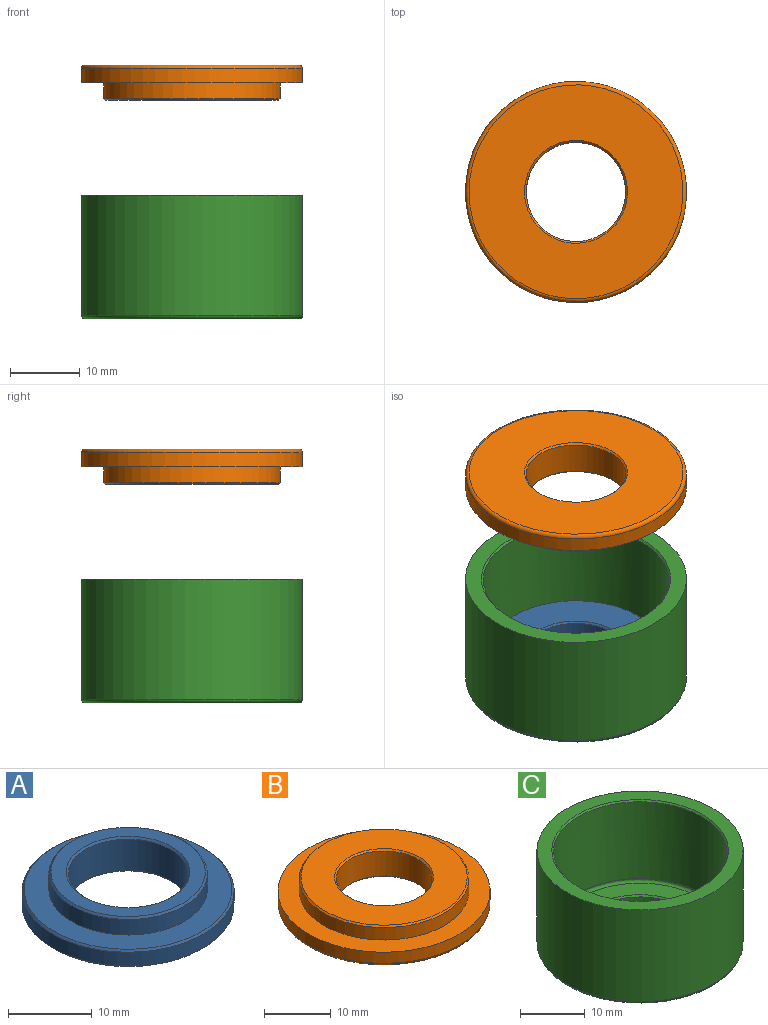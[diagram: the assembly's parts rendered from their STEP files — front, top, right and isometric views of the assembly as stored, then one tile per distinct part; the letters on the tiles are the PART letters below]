
ASSEMBLY  parts=3 mates=2
PART A: 11 faces, bbox 25.4x25.4x5.1 mm
  f0: cylinder r=12.7mm len=25.4mm, axis (0,0,-1), area 162.1mm2, adj f6,f7
  f1: plane 24.89x24.89mm, normal (0,0,1), area 203.3mm2, adj f3,f6
  f2: plane 24.89x24.89mm, normal (0,0,-1), area 314.7mm2, adj f7,f9
  f3: cylinder r=9.5mm len=18.99mm, axis (0,0,-1), area 136.4mm2, adj f1,f5
  f4: plane 18.49x18.49mm, normal (0,0,1), area 96.5mm2, adj f5,f10
  f5: cone r=9.24mm half-angle=45deg, axis (0,0,-1), area 21.1mm2, adj f3,f4
  f6: cone r=12.45mm half-angle=45deg, axis (0,0,-1), area 28.4mm2, adj f0,f1
  f7: cone r=12.7mm half-angle=45deg, axis (0,0,1), area 28.4mm2, adj f0,f2
  f8: cylinder r=7.14mm len=14.29mm, axis (0,0,-1), area 205.2mm2, adj f9,f10
  f9: cone r=7.14mm half-angle=45deg, axis (0,0,-1), area 16.4mm2, adj f2,f8
  f10: cone r=7.14mm half-angle=45deg, axis (0,0,1), area 16.4mm2, adj f4,f8
PART B: 10 faces, bbox 34.4x34.4x5.1 mm
  f0: cylinder r=15.88mm len=31.75mm, axis (0,0,-1), area 202.7mm2, adj f1,f6
  f1: plane 31.75x31.75mm, normal (0,0,1), area 285mm2, adj f0,f3
  f2: plane 30.73x30.73mm, normal (0,0,-1), area 569.9mm2, adj f6,f7
  f3: cylinder r=12.7mm len=25.4mm, axis (0,0,-1), area 182.4mm2, adj f1,f9
  f4: plane 24.89x24.89mm, normal (0,0,1), area 314.7mm2, adj f8,f9
  f5: cylinder r=7.14mm len=14.29mm, axis (0,0,-1), area 205.2mm2, adj f7,f8
  f6: torus R=15.37mm, axis (0,0,1), area 78.7mm2, adj f0,f2
  f7: cone r=7.14mm half-angle=45deg, axis (0,0,-1), area 16.4mm2, adj f2,f5
  f8: cone r=7.14mm half-angle=45deg, axis (0,0,1), area 16.4mm2, adj f4,f5
  f9: cone r=12.45mm half-angle=45deg, axis (0,0,-1), area 28.4mm2, adj f3,f4
PART C: 11 faces, bbox 34.4x34.4x17.8 mm
  f0: cylinder r=15.88mm len=31.75mm, axis (0,0,-1), area 1722.8mm2, adj f1,f6
  f1: plane 31.75x31.75mm, normal (0,0,1), area 211.6mm2, adj f0,f7
  f2: plane 30.73x30.73mm, normal (0,0,-1), area 441.4mm2, adj f6,f9
  f3: cylinder r=13.33mm len=26.67mm, axis (0,0,-1), area 1213.1mm2, adj f7,f10
  f4: plane 25.67x25.67mm, normal (0,0,1), area 216.5mm2, adj f8,f10
  f5: cylinder r=9.53mm len=19.05mm, axis (0,0,-1), area 121.6mm2, adj f8,f9
  f6: torus R=15.37mm, axis (0,0,1), area 78.7mm2, adj f0,f2
  f7: cone r=13.33mm half-angle=45deg, axis (0,0,1), area 30.4mm2, adj f1,f3
  f8: cone r=9.53mm half-angle=45deg, axis (0,0,1), area 21.8mm2, adj f4,f5
  f9: cone r=9.53mm half-angle=45deg, axis (0,0,-1), area 21.8mm2, adj f2,f5
  f10: bspline ~27.36x27.36mm, area 68.3mm2, adj f3,f4
PLACE A rot(axis=(1,0,0),180deg) t=(23.12,-17.48,-50.14)mm
PLACE B rot(axis=(0,-1,0),180deg) t=(23.12,-17.48,-18.75)mm
PLACE C t=(23.12,-17.48,-55.22)mm
MATE slider B.f0 <-> C.f0  axis (0,0,-1) through (23.12,-17.48,-21.29)mm
MATE fastened A.f0 <-> C.f0  axis (0,0,-1) through (23.12,-17.48,-52.68)mm
